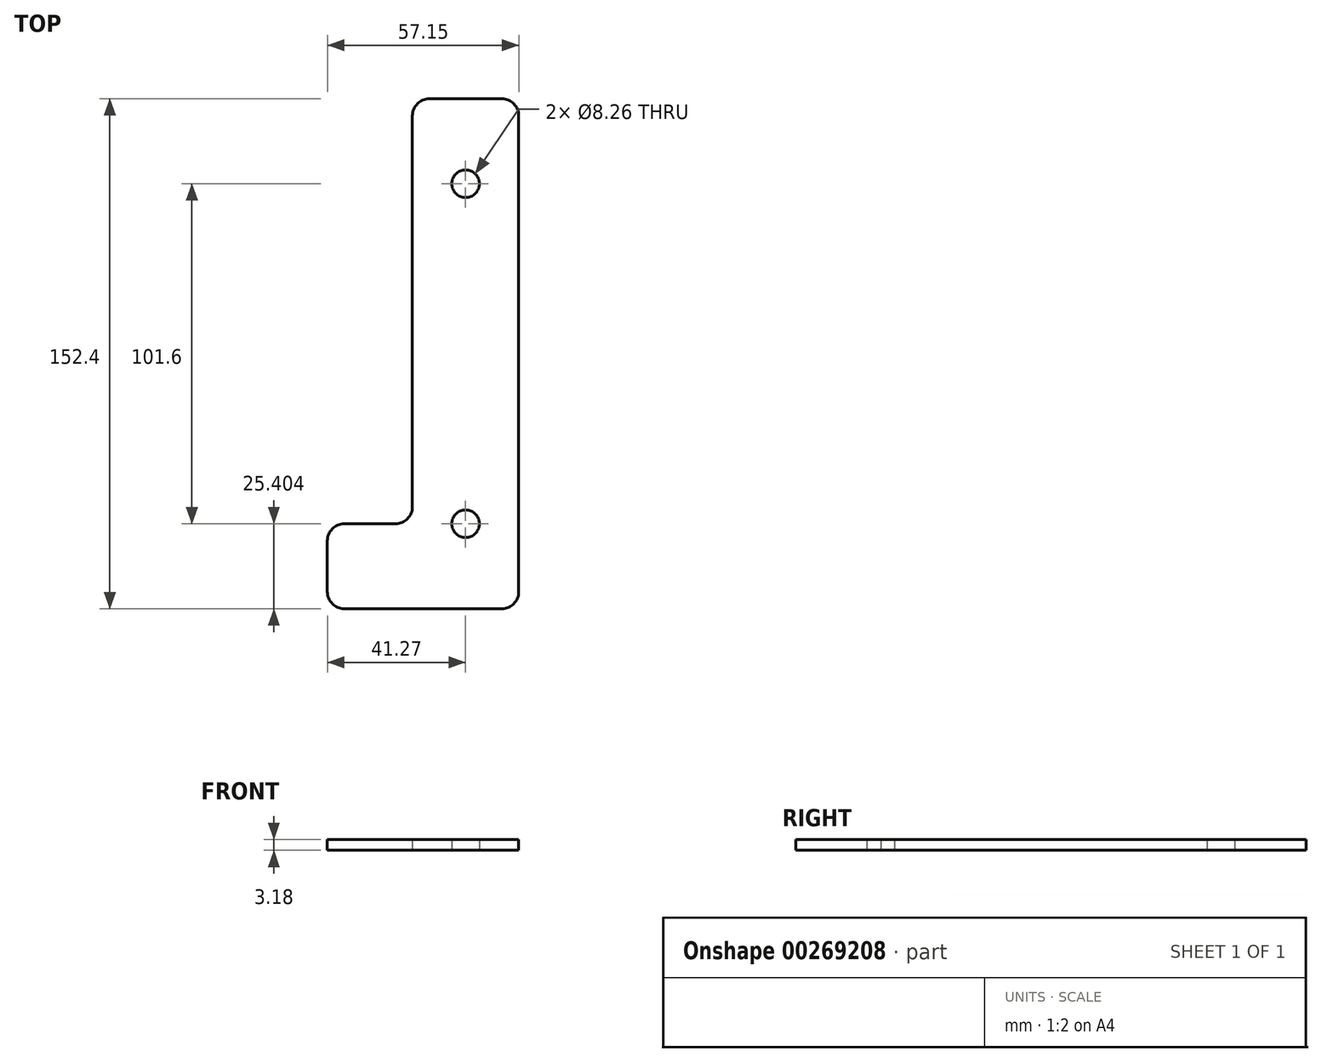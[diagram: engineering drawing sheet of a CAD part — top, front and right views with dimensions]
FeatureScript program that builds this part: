
annotation { "Feature Type Name" : "Feature", "Feature Type Description" : "" }
export const myFeature = defineFeature(function(context is Context, id is Id, definition is map)
    precondition{}
    {
        {
            var Q0;
            Q0=qCreatedBy(makeId("Top.planeOp"),FACE);
            var sketch = newSketch(context, id + "F0", { "sketchPlane" : qUnion([Q0])});
            skLineSegment(sketch, "E0", {"start": v(-15.88, 77.23) * mm, "end": v(15.88, 77.23) * mm});
            skLineSegment(sketch, "E1", {"start": v(15.88, 77.23) * mm, "end": v(15.88, -75.17) * mm});
            skLineSegment(sketch, "E2", {"start": v(15.88, -75.17) * mm, "end": v(-41.27, -75.17) * mm});
            skLineSegment(sketch, "E3", {"start": v(-41.27, -75.17) * mm, "end": v(-41.27, -49.77) * mm});
            skLineSegment(sketch, "E4", {"start": v(-41.27, -49.77) * mm, "end": v(-15.87, -49.77) * mm});
            skLineSegment(sketch, "E5", {"start": v(-15.87, -49.77) * mm, "end": v(-15.88, 77.23) * mm});
            skCircle(sketch, "E6", {"center": v(0, 51.83) * mm, "radius": 4.13 * mm});
            skCircle(sketch, "E7", {"center": v(0, -49.77) * mm, "radius": 4.13 * mm});
            skLineSegment(sketch, "E8", {"start": v(0, 77.23) * mm, "end": v(0, -75.17) * mm, "construction": true});
            skSolve(sketch);
        }
        {
            var Q0;
            Q0 = qSketchRegion(id + "F0", true);
            extrude(context, id + "F1", {"entities" : qUnion([Q0]), "depth" : 3.17 * mm});
        }
        {
            var Q0;
            Q0=makeQuery(id+"F1.opExtrude","SWEPT_EDGE",EDGE,{"disambiguationData":[OSD([sQuery(id+"F0.wireOp",EDGE,"E0"),sQuery(id+"F0.wireOp",EDGE,"E5")])]});
            var Q1;
            Q1=makeQuery(id+"F1.opExtrude","SWEPT_EDGE",EDGE,{"disambiguationData":[OSD([sQuery(id+"F0.wireOp",EDGE,"E0"),sQuery(id+"F0.wireOp",EDGE,"E1")])]});
            var Q2;
            Q2=makeQuery(id+"F1.opExtrude","SWEPT_EDGE",EDGE,{"disambiguationData":[OSD([sQuery(id+"F0.wireOp",EDGE,"E4"),sQuery(id+"F0.wireOp",EDGE,"E5")])]});
            var Q3;
            Q3=makeQuery(id+"F1.opExtrude","SWEPT_EDGE",EDGE,{"disambiguationData":[OSD([sQuery(id+"F0.wireOp",EDGE,"E3"),sQuery(id+"F0.wireOp",EDGE,"E4")])]});
            var Q4;
            Q4=makeQuery(id+"F1.opExtrude","SWEPT_EDGE",EDGE,{"disambiguationData":[OSD([sQuery(id+"F0.wireOp",EDGE,"E2"),sQuery(id+"F0.wireOp",EDGE,"E3")])]});
            var Q5;
            Q5=makeQuery(id+"F1.opExtrude","SWEPT_EDGE",EDGE,{"disambiguationData":[OSD([sQuery(id+"F0.wireOp",EDGE,"E1"),sQuery(id+"F0.wireOp",EDGE,"E2")])]});
            fillet(context, id + "F2", {"entities" : qUnion([Q0, Q1, Q2, Q3, Q4, Q5]), "radius" : 5.08 * mm, "tangentPropagation" : true, "allowEdgeOverflow" : false});
        }
    });
